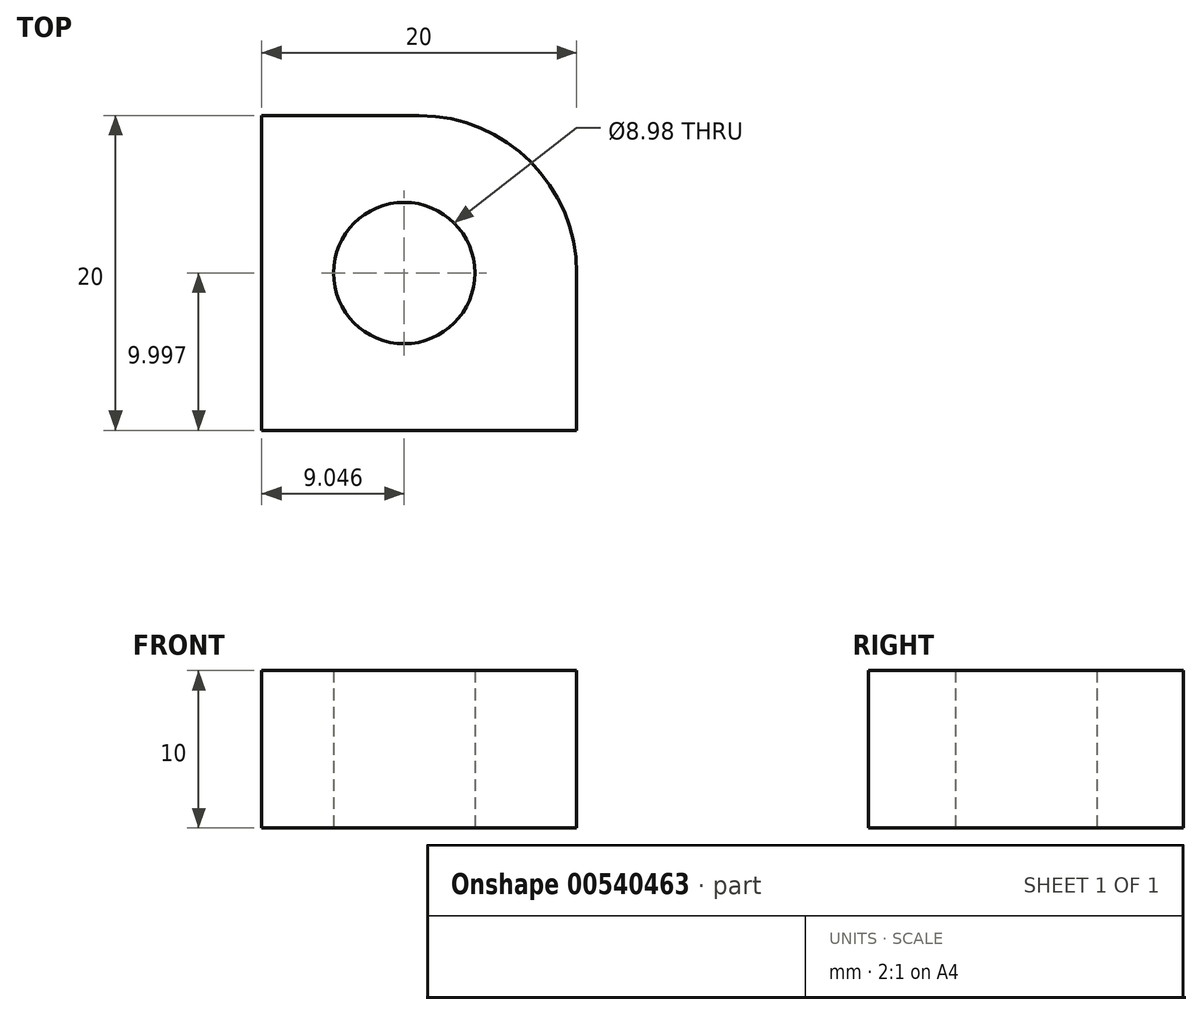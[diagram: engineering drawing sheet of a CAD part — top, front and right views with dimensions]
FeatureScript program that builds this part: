
annotation { "Feature Type Name" : "Feature", "Feature Type Description" : "" }
export const myFeature = defineFeature(function(context is Context, id is Id, definition is map)
    precondition{}
    {
        {
            var Q0;
            Q0=qCreatedBy(makeId("Top.planeOp"),FACE);
            var sketch = newSketch(context, id + "F0", { "sketchPlane" : qUnion([Q0])});
            skLineSegment(sketch, "E0.bottom", {"start": v(-5.1, 3.38) * mm, "end": v(4.9, 3.38) * mm});
            skLineSegment(sketch, "E0.top", {"start": v(-5.1, -16.62) * mm, "end": v(14.9, -16.62) * mm});
            skLineSegment(sketch, "E0.left", {"start": v(-5.1, 3.38) * mm, "end": v(-5.1, -16.62) * mm});
            skLineSegment(sketch, "E0.right", {"start": v(14.9, -6.62) * mm, "end": v(14.9, -16.62) * mm});
            skPoint(sketch, "E1.visualSharp", {"position": v(14.9, 3.38) * mm});
            skArc(sketch, "E1.filletArc", {"start": v(14.9, -6.62) * mm, "mid": v(11.96, 0.45) * mm, "end": v(4.9, 3.38) * mm});
            skCircle(sketch, "E2", {"center": v(3.94, -6.62) * mm, "radius": 4.5 * mm});
            skSolve(sketch);
        }
        {
            var Q0;
            Q0 = qSketchRegion(id + "F0", true);
            extrude(context, id + "F1", {"entities" : qUnion([Q0]), "depth" : 10 * mm, "offsetDistance" : 25 * mm});
        }
    });
